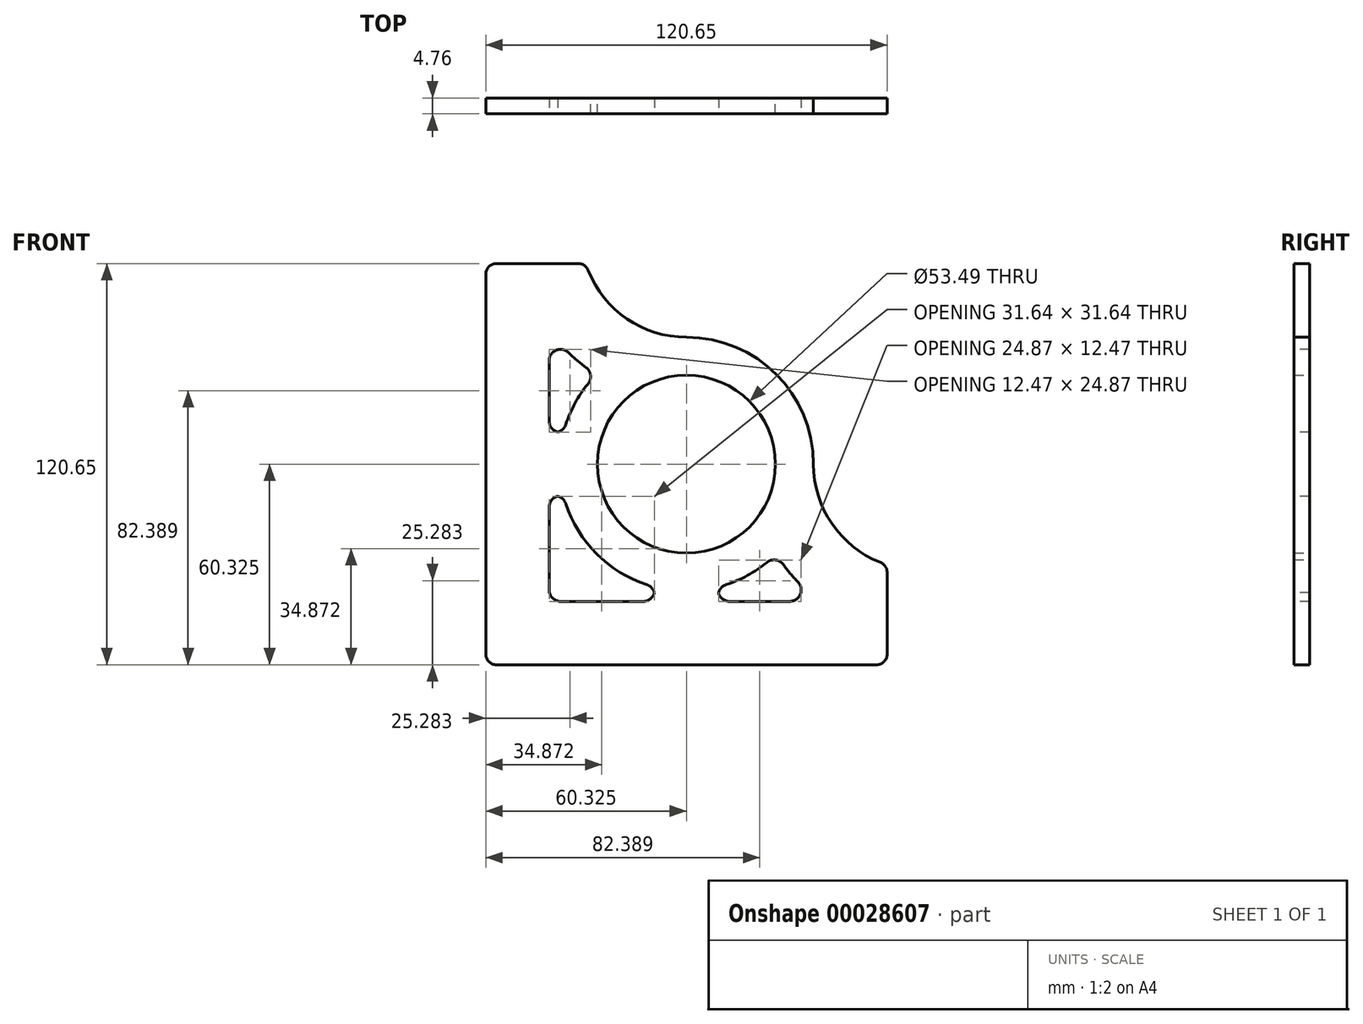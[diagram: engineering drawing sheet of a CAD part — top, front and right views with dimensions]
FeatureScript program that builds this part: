
annotation { "Feature Type Name" : "Feature", "Feature Type Description" : "" }
export const myFeature = defineFeature(function(context is Context, id is Id, definition is map)
    precondition{}
    {
        {
            var Q0;
            Q0=qCreatedBy(makeId("Front.planeOp"),FACE);
            var sketch = newSketch(context, id + "F0", { "sketchPlane" : qUnion([Q0])});
            skLineSegment(sketch, "E0.bottom", {"start": v(0, 0) * mm, "end": v(120.65, 0) * mm});
            skLineSegment(sketch, "E0.top", {"start": v(0, 120.65) * mm, "end": v(30.06, 120.65) * mm});
            skLineSegment(sketch, "E0.left", {"start": v(0, 0) * mm, "end": v(0, 120.65) * mm});
            skLineSegment(sketch, "E0.right", {"start": v(120.65, 0) * mm, "end": v(120.65, 30.06) * mm});
            skCircle(sketch, "E1", {"center": v(60.32, 60.33) * mm, "radius": 26.75 * mm});
            skCircle(sketch, "E2", {"center": v(60.32, 60.33) * mm, "radius": 38.18 * mm});
            skArc(sketch, "E3", {"start": v(30.06, 120.65) * mm, "mid": v(41.57, 104.63) * mm, "end": v(60.32, 98.5) * mm});
            skArc(sketch, "E4", {"start": v(98.5, 60.33) * mm, "mid": v(104.63, 41.57) * mm, "end": v(120.65, 30.06) * mm});
            skLineSegment(sketch, "E5", {"start": v(60.32, 60.33) * mm, "end": v(60.32, 154) * mm, "construction": true});
            skLineSegment(sketch, "E6", {"start": v(60.32, 60.33) * mm, "end": v(120.65, 60.33) * mm, "construction": true});
            skPoint(sketch, "E7.orphan", {"position": v(200.18, 60.33) * mm});
            skSolve(sketch);
        }
        {
            var Q0;
            Q0=makeQuery(id+"F0.imprint","IMPRINT",FACE,{"disambiguationData":[TD([[makeQuery(id+"F0.imprint","IMPRINT",EDGE,{"derivedFrom":sQuery(id+"F0.wireOp",EDGE,"E0.bottom")}),1.0]])]});
            var Q1;
            Q1=makeQuery(id+"F0.imprint","IMPRINT",FACE,{"disambiguationData":[TD([[makeQuery(id+"F0.imprint","IMPRINT",EDGE,{"derivedFrom":sQuery(id+"F0.wireOp",EDGE,"E1")}),-1.0]])]});
            extrude(context, id + "F1", {"entities" : qUnion([Q0, Q1]), "depth" : 4.76 * mm});
        }
        {
            var Q0;
            Q0=makeQuery(id+"F1.opExtrude","CAP_FACE",FACE,{"disambiguationData":[OSD([sQuery(id+"F0.wireOp",EDGE,"E0.bottom"),sQuery(id+"F0.wireOp",EDGE,"E0.top"),sQuery(id+"F0.wireOp",EDGE,"E0.left"),sQuery(id+"F0.wireOp",EDGE,"E0.right"),sQuery(id+"F0.wireOp",EDGE,"E1"),sQuery(id+"F0.wireOp",EDGE,"E2"),sQuery(id+"F0.wireOp",EDGE,"E3"),sQuery(id+"F0.wireOp",EDGE,"E4")])],"isStart":false});
            var sketch = newSketch(context, id + "F2", { "sketchPlane" : qUnion([Q0])});
            skLineSegment(sketch, "E8.0", {"start": v(19.05, 101.6) * mm, "end": v(18.38, 101.6) * mm});
            skArc(sketch, "E8.1", {"start": v(33.27, 87.26) * mm, "mid": v(25.08, 93.66) * mm, "end": v(18.38, 101.6) * mm});
            skArc(sketch, "E8.3", {"start": v(101.6, 18.38) * mm, "mid": v(93.66, 25.08) * mm, "end": v(87.26, 33.27) * mm});
            skLineSegment(sketch, "E8.4", {"start": v(101.6, 18.38) * mm, "end": v(101.6, 19.05) * mm});
            skLineSegment(sketch, "E8.5", {"start": v(19.05, 101.6) * mm, "end": v(19.05, 69.85) * mm});
            skLineSegment(sketch, "E8.6", {"start": v(19.05, 19.05) * mm, "end": v(50.8, 19.05) * mm});
            skArc(sketch, "E9", {"start": v(33.27, 87.26) * mm, "mid": v(27.15, 79.21) * mm, "end": v(23.36, 69.85) * mm});
            skLineSegment(sketch, "E10.left", {"start": v(50.8, 19.05) * mm, "end": v(50.8, 23.36) * mm});
            skLineSegment(sketch, "E10.right", {"start": v(69.85, 19.05) * mm, "end": v(69.85, 23.36) * mm});
            skLineSegment(sketch, "E11", {"start": v(60.32, 60.33) * mm, "end": v(60.32, 2.5) * mm, "construction": true});
            skArc(sketch, "E12.trimOffspring", {"start": v(69.85, 23.36) * mm, "mid": v(79.21, 27.15) * mm, "end": v(87.26, 33.27) * mm});
            skLineSegment(sketch, "E13.trimOffspring", {"start": v(69.85, 19.05) * mm, "end": v(101.6, 19.05) * mm});
            skLineSegment(sketch, "E14", {"start": v(60.32, 60.33) * mm, "end": v(-46.2, 60.32) * mm, "construction": true});
            skLineSegment(sketch, "E15.bottom", {"start": v(23.36, 69.85) * mm, "end": v(19.05, 69.85) * mm});
            skLineSegment(sketch, "E15.top", {"start": v(23.36, 50.8) * mm, "end": v(19.05, 50.8) * mm});
            skArc(sketch, "E16.trimOffspring", {"start": v(23.36, 50.8) * mm, "mid": v(33.33, 33.33) * mm, "end": v(50.8, 23.36) * mm});
            skLineSegment(sketch, "E17.trimOffspring", {"start": v(19.05, 50.8) * mm, "end": v(19.05, 19.05) * mm});
            skSolve(sketch);
        }
        {
            var Q0;
            {var subQ1=sQuery(id+"F2.wireOp",EDGE,"E9");Q0=makeQuery(id+"F2.imprint","IMPRINT",FACE,{"disambiguationData":[TD([[makeQuery(id+"F2.imprint","IMPRINT",EDGE,{"derivedFrom":subQ1}),-1.0]])]});}
            var Q1;
            Q1=makeQuery(id+"F2.imprint","IMPRINT",FACE,{"disambiguationData":[TD([[makeQuery(id+"F2.imprint","IMPRINT",EDGE,{"derivedFrom":sQuery(id+"F2.wireOp",EDGE,"E8.6")}),1.0]])]});
            var Q2;
            {var subQ3=sQuery(id+"F2.wireOp",EDGE,"E10.right");Q2=makeQuery(id+"F2.imprint","IMPRINT",FACE,{"disambiguationData":[TD([[makeQuery(id+"F2.imprint","IMPRINT",EDGE,{"derivedFrom":subQ3}),-1.0]])]});}
            extrude(context, id + "F3", {"entities" : qUnion([Q0, Q1, Q2]), "operationType" : NewBodyOperationType.REMOVE, "endBound" : BoundingType.THROUGH_ALL, "oppositeDirection" : true, "depth" : 25.4 * mm});
        }
        {
            var Q0;
            Q0=makeQuery(id+"F3.boolean.opBoolean","COPY",EDGE,{"derivedFrom":makeQuery(id+"F3.opExtrude","SWEPT_EDGE",EDGE,{"disambiguationData":[OSD([sQuery(id+"F2.wireOp",EDGE,"E8.1"),sQuery(id+"F2.wireOp",EDGE,"E8.5")])]})});
            var Q1;
            Q1=makeQuery(id+"F3.boolean.opBoolean","COPY",EDGE,{"derivedFrom":makeQuery(id+"F3.opExtrude","SWEPT_EDGE",EDGE,{"disambiguationData":[OSD([sQuery(id+"F2.wireOp",EDGE,"E8.1"),sQuery(id+"F2.wireOp",EDGE,"E9")])]})});
            var Q2;
            Q2=makeQuery(id+"F3.boolean.opBoolean","COPY",EDGE,{"derivedFrom":makeQuery(id+"F3.opExtrude","SWEPT_EDGE",EDGE,{"disambiguationData":[OSD([sQuery(id+"F2.wireOp",EDGE,"E9"),sQuery(id+"F2.wireOp",EDGE,"E15.bottom")])]})});
            var Q3;
            Q3=makeQuery(id+"F3.boolean.opBoolean","COPY",EDGE,{"derivedFrom":makeQuery(id+"F3.opExtrude","SWEPT_EDGE",EDGE,{"disambiguationData":[OSD([sQuery(id+"F2.wireOp",EDGE,"E8.5"),sQuery(id+"F2.wireOp",EDGE,"E15.bottom")])]})});
            var Q4;
            Q4=makeQuery(id+"F3.boolean.opBoolean","COPY",EDGE,{"derivedFrom":makeQuery(id+"F3.opExtrude","SWEPT_EDGE",EDGE,{"disambiguationData":[OSD([sQuery(id+"F2.wireOp",EDGE,"E10.left"),sQuery(id+"F2.wireOp",EDGE,"E16.trimOffspring")])]})});
            var Q5;
            Q5=makeQuery(id+"F3.boolean.opBoolean","COPY",EDGE,{"derivedFrom":makeQuery(id+"F3.opExtrude","SWEPT_EDGE",EDGE,{"disambiguationData":[OSD([sQuery(id+"F2.wireOp",EDGE,"E8.6"),sQuery(id+"F2.wireOp",EDGE,"E10.left")])]})});
            var Q6;
            Q6=makeQuery(id+"F3.boolean.opBoolean","COPY",EDGE,{"derivedFrom":makeQuery(id+"F3.opExtrude","SWEPT_EDGE",EDGE,{"disambiguationData":[OSD([sQuery(id+"F2.wireOp",EDGE,"E15.top"),sQuery(id+"F2.wireOp",EDGE,"E16.trimOffspring")])]})});
            var Q7;
            Q7=makeQuery(id+"F3.boolean.opBoolean","COPY",EDGE,{"derivedFrom":makeQuery(id+"F3.opExtrude","SWEPT_EDGE",EDGE,{"disambiguationData":[OSD([sQuery(id+"F2.wireOp",EDGE,"E8.6"),sQuery(id+"F2.wireOp",EDGE,"E17.trimOffspring")])]})});
            var Q8;
            Q8=makeQuery(id+"F3.boolean.opBoolean","COPY",EDGE,{"derivedFrom":makeQuery(id+"F3.opExtrude","SWEPT_EDGE",EDGE,{"disambiguationData":[OSD([sQuery(id+"F2.wireOp",EDGE,"E15.top"),sQuery(id+"F2.wireOp",EDGE,"E17.trimOffspring")])]})});
            var Q9;
            Q9=makeQuery(id+"F3.boolean.opBoolean","COPY",EDGE,{"derivedFrom":makeQuery(id+"F3.opExtrude","SWEPT_EDGE",EDGE,{"disambiguationData":[OSD([sQuery(id+"F2.wireOp",EDGE,"E10.right"),sQuery(id+"F2.wireOp",EDGE,"E12.trimOffspring")])]})});
            var Q10;
            Q10=makeQuery(id+"F3.boolean.opBoolean","COPY",EDGE,{"derivedFrom":makeQuery(id+"F3.opExtrude","SWEPT_EDGE",EDGE,{"disambiguationData":[OSD([sQuery(id+"F2.wireOp",EDGE,"E10.right"),sQuery(id+"F2.wireOp",EDGE,"E13.trimOffspring")])]})});
            var Q11;
            Q11=makeQuery(id+"F3.boolean.opBoolean","COPY",EDGE,{"derivedFrom":makeQuery(id+"F3.opExtrude","SWEPT_EDGE",EDGE,{"disambiguationData":[OSD([sQuery(id+"F2.wireOp",EDGE,"E8.3"),sQuery(id+"F2.wireOp",EDGE,"E12.trimOffspring")])]})});
            var Q12;
            Q12=makeQuery(id+"F3.boolean.opBoolean","COPY",EDGE,{"derivedFrom":makeQuery(id+"F3.opExtrude","SWEPT_EDGE",EDGE,{"disambiguationData":[OSD([sQuery(id+"F2.wireOp",EDGE,"E8.3"),sQuery(id+"F2.wireOp",EDGE,"E13.trimOffspring")])]})});
            fillet(context, id + "F4", {"entities" : qUnion([Q0, Q1, Q2, Q3, Q4, Q5, Q6, Q7, Q8, Q9, Q10, Q11, Q12]), "radius" : 3.43 * mm, "tangentPropagation" : true, "allowEdgeOverflow" : false});
        }
        {
            var Q0;
            Q0=makeQuery(id+"F1.opExtrude","SWEPT_EDGE",EDGE,{"disambiguationData":[OSD([sQuery(id+"F0.wireOp",EDGE,"E0.right"),sQuery(id+"F0.wireOp",EDGE,"E4")])]});
            var Q1;
            Q1=makeQuery(id+"F1.opExtrude","SWEPT_EDGE",EDGE,{"disambiguationData":[OSD([sQuery(id+"F0.wireOp",EDGE,"E0.bottom"),sQuery(id+"F0.wireOp",EDGE,"E0.right")])]});
            var Q2;
            Q2=makeQuery(id+"F1.opExtrude","SWEPT_EDGE",EDGE,{"disambiguationData":[OSD([sQuery(id+"F0.wireOp",EDGE,"E0.top"),sQuery(id+"F0.wireOp",EDGE,"E3")])]});
            var Q3;
            Q3=makeQuery(id+"F1.opExtrude","SWEPT_EDGE",EDGE,{"disambiguationData":[OSD([sQuery(id+"F0.wireOp",EDGE,"E0.top"),sQuery(id+"F0.wireOp",EDGE,"E0.left")])]});
            var Q4;
            Q4=makeQuery(id+"F1.opExtrude","SWEPT_EDGE",EDGE,{"disambiguationData":[OSD([sQuery(id+"F0.wireOp",EDGE,"E0.bottom"),sQuery(id+"F0.wireOp",EDGE,"E0.left")])]});
            fillet(context, id + "F5", {"entities" : qUnion([Q0, Q1, Q2, Q3, Q4]), "radius" : 3.17 * mm, "tangentPropagation" : true, "allowEdgeOverflow" : false});
        }
    });
